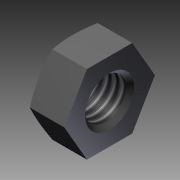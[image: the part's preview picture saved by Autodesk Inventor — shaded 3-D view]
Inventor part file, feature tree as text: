
AUTODESK INVENTOR PART (.ipt)
format: ipt  version: 2011 SP1 (Build 150282100, 282)  size: 105,472 bytes
history: native  units: mm
features: other x7, sketch x2, revolve x1, thread x1, extrude x1
ambient origin geometry x8: Origin, YZ Plane, XZ Plane, XY Plane, X Axis, Y Axis, Z Axis, Center Point
bodies: Solid1 (feature_tree)
feature tree (12):
  revolve  "Revolution1"  [1 undecoded]
  thread  "Thread1"  [1 undecoded]
  extrude  "Extrusion1"  [1 undecoded]
  other  "nut_to_pad_XY"
  other  "nut_to_pad_YZ"
  other  "nut_to_pad_ZX"
  other  "nut_to_pad_X"
  other  "nut_to_pad_Y"
  other  "nut_to_pad_Z"
  other  "nut_to_pad_Center"
  sketch  "Sketch_1"  dims[d0=360.0deg d1=3.134mm d2=0.0mm d3=4.0mm d4=0.0mm]
  sketch  "Sketch_2"  dims[d5=0.0mm]
note: 3 required parameter values undecoded (feature->parameter linkage not recoverable at this tier; creation-order binding heuristic only, values carry confidence <= 0.55)